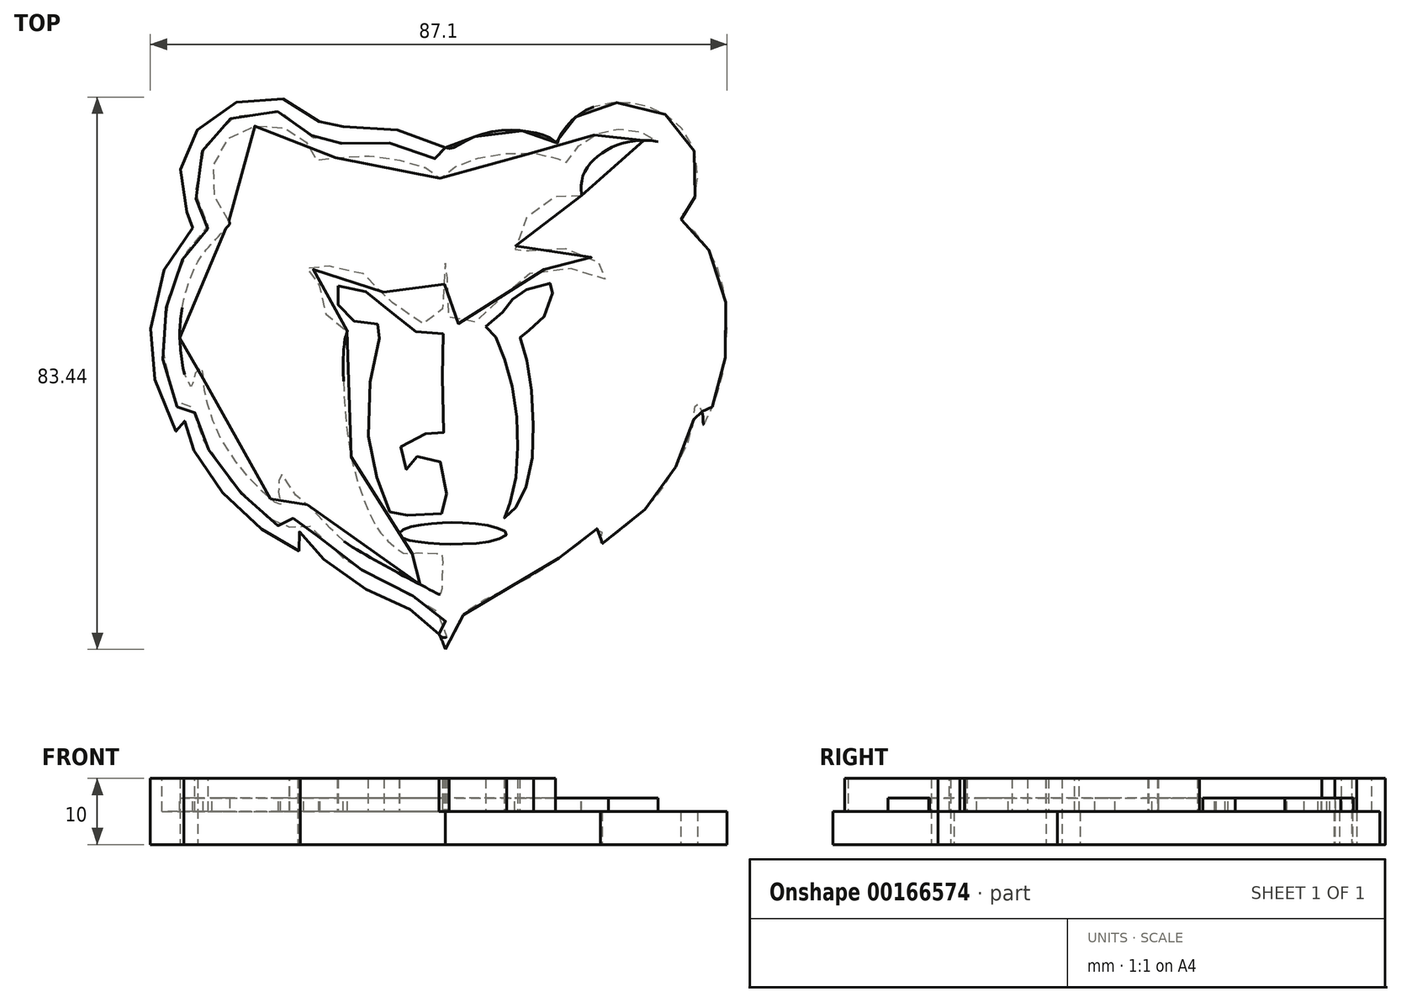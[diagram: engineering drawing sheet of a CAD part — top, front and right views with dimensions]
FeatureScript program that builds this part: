
annotation { "Feature Type Name" : "Feature", "Feature Type Description" : "" }
export const myFeature = defineFeature(function(context is Context, id is Id, definition is map)
    precondition{}
    {
        {
            var Q0;
            Q0=qCreatedBy(makeId("Top.planeOp"),FACE);
            var sketch = newSketch(context, id + "F0", { "sketchPlane" : qUnion([Q0])});
            skLineSegment(sketch, "E0", {"start": v(0, 41.26) * mm, "end": v(0, -52.03) * mm, "construction": true});
            skFitSpline(sketch, "E1", {"points": [v(0, 27.13) * mm, v(-4.89, 29.17) * mm, v(-10.68, 30.33) * mm, v(-16.3, 30.11) * mm, v(-17.96, 29.67) * mm, v(-18.3, 30.11) * mm, v(-20.17, 32.15) * mm, v(-23.48, 34.2) * mm, v(-27.3, 34.75) * mm, v(-32.15, 33.8) * mm, v(-36.17, 31.38) * mm, v(-38.93, 27.4) * mm, v(-39.93, 24.26) * mm, v(-39.87, 19.57) * mm, v(-38.93, 17.14) * mm, v(-38.1, 15.82) * mm, v(-37.39, 15.27) * mm, v(-38.16, 15.05) * mm, v(-40.75, 11.96) * mm, v(-43.84, 4.9) * mm, v(-44.56, -1.84) * mm, v(-44.12, -6.92) * mm, v(-41.75, -13.87) * mm, v(-40.04, -16.4) * mm, v(-39.54, -16.4) * mm, v(-39.65, -15.52) * mm, v(-39.32, -14.09) * mm, v(-39.1, -15.52) * mm, v(-38.1, -18.4) * mm, v(-35.57, -22.42) * mm, v(-31.81, -27.06) * mm, v(-27.4, -30.8) * mm, v(-23.76, -33.18) * mm, v(-21.94, -33.79) * mm, v(-22.16, -33.13) * mm, v(-22.32, -31.97) * mm, v(-22.1, -30.92) * mm, v(-21, -32.3) * mm, v(-18.74, -34.73) * mm, v(-14.6, -38.1) * mm, v(-9.9, -40.58) * mm, v(-5.6, -42.5) * mm, v(-2.68, -44.33) * mm, v(-0.97, -46.42) * mm, v(0, -48.69) * mm], "startDerivative": vector(-162.67, 75.76) * mm, "endDerivative": vector(42.07, -115.13) * mm});
            skFitSpline(sketch, "E2", {"points": [v(0, -48.69) * mm, v(1, -46.59) * mm, v(2.6, -43.61) * mm, v(5.27, -41.5) * mm, v(12.4, -37.98) * mm, v(16.97, -35) * mm, v(21.87, -31.35) * mm, v(22.98, -30.42) * mm, v(23.54, -30.8) * mm, v(23.6, -32.03) * mm, v(23.42, -32.84) * mm, v(25.52, -31.35) * mm, v(30.35, -27.32) * mm, v(33.39, -23.42) * mm, v(36.24, -18.4) * mm, v(37.49, -14.1) * mm, v(37.88, -11.34) * mm, v(38.1, -11.43) * mm, v(38.63, -12.26) * mm, v(38.94, -13.97) * mm, v(39.02, -14.76) * mm, v(40.47, -11.65) * mm, v(41.83, -7.31) * mm, v(42.5, -1.49) * mm, v(42.28, 4.04) * mm, v(40.8, 9.7) * mm, v(38.07, 13.97) * mm, v(35.8, 16.07) * mm, v(35.59, 16.42) * mm, v(35.63, 16.95) * mm, v(36.5, 17.78) * mm, v(37.82, 20.19) * mm, v(37.94, 24.7) * mm, v(37.11, 27.8) * mm, v(34.47, 31.27) * mm, v(30.13, 33.46) * mm, v(25.54, 33.92) * mm, v(21.74, 33) * mm, v(18.92, 31.06) * mm, v(17.1, 28.46) * mm, v(16.9, 27.8) * mm, v(15.99, 28.46) * mm, v(13.67, 29.33) * mm, v(10.33, 29.78) * mm, v(5.78, 29.24) * mm, v(2.35, 27.76) * mm, v(0.86, 27.01) * mm, v(0, 27.13) * mm], "startDerivative": vector(49.23, 102.83) * mm, "endDerivative": vector(-71.58, 21.7) * mm});
            skFitSpline(sketch, "E3", {"points": [v(0, 27.13) * mm, v(0.32, 26.7) * mm, v(0.53, 25.95) * mm, v(0.24, 25.3) * mm, v(-0.9, 25.22) * mm, v(-2.84, 26.07) * mm, v(-5.73, 27.13) * mm, v(-9.87, 28.03) * mm, v(-13.28, 28.07) * mm, v(-15.78, 27.78) * mm, v(-17.43, 27.45) * mm, v(-18.61, 27.33) * mm, v(-19.96, 28.65) * mm, v(-21.65, 30.58) * mm, v(-23.82, 32.04) * mm, v(-26.18, 32.7) * mm, v(-29.9, 32.41) * mm, v(-32.48, 31.5) * mm, v(-34.55, 29.87) * mm, v(-36.12, 27.74) * mm, v(-37.34, 25.12) * mm, v(-37.85, 21.65) * mm, v(-37.48, 18.46) * mm, v(-36.66, 16.5) * mm, v(-36, 15.61) * mm, v(-35.85, 15.05) * mm, v(-36.18, 14.62) * mm, v(-37.17, 13.8) * mm, v(-39.03, 11.41) * mm, v(-40.7, 8.1) * mm, v(-41.71, 4.92) * mm, v(-42.56, 0.72) * mm, v(-42.78, -2.61) * mm, v(-42.43, -6.62) * mm, v(-41.2, -10.52) * mm, v(-40.42, -12.14) * mm, v(-40.24, -12.18) * mm, v(-39.67, -11.66) * mm, v(-38.9, -11.5) * mm, v(-38.18, -12.27) * mm, v(-37.68, -13.36) * mm, v(-37.29, -14.98) * mm, v(-36.34, -17.54) * mm, v(-34.69, -20.14) * mm, v(-32.23, -23.5) * mm, v(-29.14, -26.86) * mm, v(-26.99, -28.72) * mm, v(-24.55, -30.58) * mm, v(-23.74, -31.1) * mm, v(-23.55, -31.02) * mm, v(-23.55, -30.02) * mm, v(-22.9, -28.81) * mm, v(-22.05, -28.65) * mm, v(-21, -29.44) * mm, v(-19.6, -31.16) * mm, v(-17.43, -33.45) * mm, v(-13.55, -36.17) * mm, v(-8.98, -38.6) * mm, v(-5.16, -40.51) * mm, v(-2.53, -41.94) * mm, v(-0.74, -43.42) * mm, v(0.17, -44.7) * mm, v(0.5, -45.67) * mm, v(0.36, -46.67) * mm, v(-0.4, -46.89) * mm, v(-0.97, -46.42) * mm], "startDerivative": vector(43.35, -47.73) * mm, "endDerivative": vector(-53.4, 65.08) * mm});
            skSolve(sketch);
        }
        {
            var Q0;
            Q0 = qSketchRegion(id + "F0", true);
            extrude(context, id + "F1", {"entities" : qUnion([Q0]), "depth" : 5 * mm});
        }
        {
            var Q0;
            {var subQ0=sQuery(id+"F0.wireOp",EDGE,"E3");Q0=makeQuery(id+"F0.imprint","IMPRINT",FACE,{"disambiguationData":[TD([[makeQuery(id+"F0.imprint","IMPRINT",EDGE,{"derivedFrom":subQ0}),-1.0]])]});}
            extrude(context, id + "F2", {"entities" : qUnion([Q0]), "operationType" : NewBodyOperationType.ADD, "depth" : 10 * mm});
        }
        {
            var Q0;
            Q0=makeQuery(id+"F1.opExtrude","CAP_FACE",FACE,{"disambiguationData":[OSD([sQuery(id+"F0.wireOp",EDGE,"E1"),sQuery(id+"F0.wireOp",EDGE,"E2")])],"isStart":false});
            var sketch = newSketch(context, id + "F3", { "sketchPlane" : qUnion([Q0])});
            skFitSpline(sketch, "E4", {"points": [v(-32.42, 15.69) * mm, v(-34.04, 17.77) * mm, v(-35.18, 21.16) * mm, v(-34.87, 24.96) * mm, v(-33.3, 28.03) * mm, v(-30.34, 29.96) * mm, v(-26.95, 30.53) * mm, v(-24.09, 30.01) * mm, v(-21.85, 28.69) * mm, v(-20.17, 26.92) * mm, v(-19.45, 25.48) * mm, v(-19.31, 25.13) * mm, v(-18.15, 25.32) * mm, v(-14.71, 25.8) * mm, v(-10.96, 25.85) * mm, v(-7.32, 25.32) * mm, v(-4.6, 24.65) * mm, v(-2.42, 23.81) * mm, v(-1.12, 22.85) * mm, v(-0.65, 22.46) * mm, v(-0.23, 22.87) * mm, v(1.03, 23.97) * mm, v(2.93, 24.93) * mm, v(5.36, 25.68) * mm, v(8.07, 26.15) * mm, v(11.57, 26.34) * mm, v(14.22, 26.2) * mm, v(16.32, 25.76) * mm, v(17.47, 25.13) * mm, v(17.89, 24.74) * mm, v(18.08, 24.57) * mm, v(18.47, 25.2) * mm, v(19.3, 26.42) * mm, v(20.55, 27.77) * mm, v(22.13, 28.85) * mm, v(23.68, 29.52) * mm, v(25.5, 29.9) * mm, v(27.57, 29.9) * mm, v(29.35, 29.58) * mm, v(31.16, 28.76) * mm, v(32.13, 28.06) * mm, v(31.46, 28.15) * mm, v(30.14, 28.24) * mm, v(27.77, 28.03) * mm, v(25.38, 27.3) * mm, v(23.07, 25.87) * mm, v(21.55, 24.35) * mm, v(20.7, 22.56) * mm, v(20.52, 20.75) * mm, v(20.55, 19.88) * mm, v(20.38, 19.61) * mm, v(19.2, 19.82) * mm, v(17.04, 19.79) * mm, v(14.68, 18.91) * mm, v(12.75, 17.16) * mm, v(11.4, 15.2) * mm, v(10.64, 12.6) * mm, v(10.52, 11.26) * mm, v(10.52, 10.57) * mm, v(11.03, 10.82) * mm, v(12.56, 11.53) * mm, v(15.19, 12.05) * mm, v(17.91, 11.95) * mm, v(20.6, 11.24) * mm, v(22.8, 10.06) * mm, v(24.28, 8.56) * mm, v(24.6, 7.65) * mm, v(24.55, 7.2) * mm, v(23.6, 7.45) * mm, v(21.28, 8.34) * mm, v(18.3, 8.93) * mm, v(14.72, 8.66) * mm, v(11.62, 7.48) * mm, v(9.68, 5.7) * mm, v(7.79, 3.67) * mm, v(5.72, 1.6) * mm, v(4.05, 0.64) * mm, v(1.94, 0.54) * mm, v(0.76, 1.11) * mm, v(0.39, 2.34) * mm, v(0.32, 5.14) * mm, v(0.3, 10) * mm, v(0.22, 11) * mm, v(0, 9.98) * mm, v(-0.2, 5.12) * mm, v(-0.52, 2.29) * mm, v(-1.06, 1.2) * mm, v(-2.27, 0.6) * mm, v(-4.38, 0.7) * mm, v(-6.76, 2.27) * mm, v(-9.15, 5.07) * mm, v(-11.56, 7.45) * mm, v(-13.74, 8.68) * mm, v(-16.13, 9.12) * mm, v(-18.8, 9.22) * mm, v(-21.17, 9.07) * mm, v(-21.39, 8.98) * mm, v(-20.11, 8.75) * mm, v(-19.32, 8.34) * mm, v(-18.98, 7.7) * mm, v(-19.08, 5.83) * mm, v(-19, 4.16) * mm, v(-18.37, 2.51) * mm, v(-17.4, 1.04) * mm, v(-16.42, 0) * mm, v(-15.12, -0.49) * mm, v(-14.83, -0.49) * mm, v(-15.02, -1.3) * mm, v(-15.4, -3.95) * mm, v(-15.4, -7.91) * mm, v(-15.08, -13.45) * mm, v(-14.42, -18.64) * mm, v(-13.2, -23.5) * mm, v(-11.2, -28.67) * mm, v(-9.59, -31.34) * mm, v(-7.55, -33.32) * mm, v(-6, -34.25) * mm, v(-4.7, -34.12) * mm, v(-3.06, -34.15) * mm, v(-0.95, -34.19) * mm, v(-0.52, -34.34) * mm, v(-0.48, -37.25) * mm, v(-0.6, -40.2) * mm, v(-0.83, -40.38) * mm, v(-2.51, -39.6) * mm, v(-6.55, -37.47) * mm, v(-11.05, -34.96) * mm, v(-15.23, -32.4) * mm, v(-18.5, -29.26) * mm, v(-21.05, -26.7) * mm, v(-22.9, -25.05) * mm, v(-24.15, -22.97) * mm, v(-24.86, -22.23) * mm, v(-25.1, -22.97) * mm, v(-25.23, -24.5) * mm, v(-24.92, -26.6) * mm, v(-24.92, -26.97) * mm, v(-26.72, -25.7) * mm, v(-29.4, -23.04) * mm, v(-33.75, -17.21) * mm, v(-35.7, -12.38) * mm, v(-36.38, -9.63) * mm, v(-36.6, -6.62) * mm, v(-36.69, -6.13) * mm, v(-37.37, -6.31) * mm, v(-37.96, -7.52) * mm, v(-38.17, -8.76) * mm, v(-38.2, -9.13) * mm, v(-38.92, -8.36) * mm, v(-39.85, -4.76) * mm, v(-40.13, -1.02) * mm, v(-39.85, 2.3) * mm, v(-38.86, 6.5) * mm, v(-37.1, 10.35) * mm, v(-35.3, 12.6) * mm, v(-33.13, 14.93) * mm], "startDerivative": vector(-236.1, 263.18) * mm, "endDerivative": vector(281.53, 298.53) * mm});
            skFitSpline(sketch, "E5", {"points": [v(-33.13, 14.93) * mm, v(-32.42, 15.69) * mm], "startDerivative": vector(0.7, 0.76) * mm, "endDerivative": vector(0.7, 0.76) * mm});
            skArc(sketch, "E6.filletArc", {"start": v(-32.73, 15.36) * mm, "mid": v(-32.6, 15.69) * mm, "end": v(-32.72, 16.03) * mm});
            skSolve(sketch);
        }
        {
            var Q0;
            Q0 = qSketchRegion(id + "F3", true);
            extrude(context, id + "F4", {"entities" : qUnion([Q0]), "operationType" : NewBodyOperationType.ADD, "depth" : 2 * mm});
        }
        {
            var Q0;
            Q0=makeQuery(id+"F1.opExtrude","CAP_FACE",FACE,{"disambiguationData":[OSD([sQuery(id+"F0.wireOp",EDGE,"E1"),sQuery(id+"F0.wireOp",EDGE,"E2")])],"isStart":false});
            var sketch = newSketch(context, id + "F5", { "sketchPlane" : qUnion([Q0])});
            skFitSpline(sketch, "E7", {"points": [v(-16.18, 6.26) * mm, v(-15.05, 6.28) * mm, v(-12.77, 5.66) * mm, v(-10.48, 4.54) * mm, v(-8.45, 2.58) * mm, v(-6.45, 0.67) * mm, v(-4.9, -0.47) * mm, v(-2.9, -1.02) * mm, v(-0.55, -1.05) * mm, v(-0.35, -1.01) * mm, v(-0.4, -3.03) * mm, v(-0.43, -10.49) * mm, v(-0.23, -16.35) * mm, v(-0.22, -16.58) * mm, v(-0.85, -16.3) * mm, v(-3.02, -16.14) * mm, v(-5.05, -16.55) * mm, v(-6.58, -17.8) * mm, v(-6.92, -19.27) * mm, v(-6.55, -20.7) * mm, v(-5.77, -21.6) * mm, v(-5.59, -21.64) * mm, v(-5.45, -20.86) * mm, v(-4.64, -19.77) * mm, v(-3.45, -19.33) * mm, v(-1.85, -19.46) * mm, v(-0.68, -20.5) * mm, v(-0.2, -21.71) * mm, v(0.2, -25.49) * mm, v(0.19, -27.61) * mm, v(0, -27.96) * mm, v(-0.4, -28.12) * mm, v(-2.68, -28.38) * mm, v(-5.63, -28.44) * mm, v(-7.22, -28.44) * mm, v(-7.92, -28.48) * mm, v(-8.08, -28.44) * mm, v(-8.6, -27.46) * mm, v(-9.82, -24.44) * mm, v(-10.92, -20.68) * mm, v(-11.63, -16.27) * mm, v(-11.5, -9.23) * mm, v(-10.5, -3.46) * mm, v(-9.67, -0.96) * mm, v(-9.3, 0) * mm, v(-9.32, 0.3) * mm, v(-10.26, 0.44) * mm, v(-11.52, 0.37) * mm, v(-12.95, 0.47) * mm, v(-14.36, 1.33) * mm, v(-15.42, 2.17) * mm, v(-15.99, 2.8) * mm, v(-16.32, 4.34) * mm, v(-16.23, 5.23) * mm, v(-16.22, 6.02) * mm, v(-16.18, 6.26) * mm]});
            skFitSpline(sketch, "E8", {"points": [v(-5.15, -30.18) * mm, v(-2.92, -29.79) * mm, v(-0.34, -29.54) * mm, v(1.7, -29.55) * mm, v(5.3, -29.8) * mm, v(8, -30.38) * mm, v(9.06, -30.88) * mm, v(9.27, -31.3) * mm, v(8.3, -31.9) * mm, v(5.73, -32.55) * mm, v(1.72, -32.77) * mm, v(-1.13, -32.75) * mm, v(-3.8, -32.46) * mm, v(-5.4, -32.22) * mm, v(-6.62, -31.78) * mm, v(-7, -31.22) * mm, v(-6.55, -30.67) * mm, v(-5.15, -30.18) * mm]});
            skFitSpline(sketch, "E9", {"points": [v(6.08, 0.08) * mm, v(7.87, 1.63) * mm, v(9.21, 2.89) * mm, v(9.94, 3.94) * mm, v(10.5, 4.7) * mm, v(11.78, 5.46) * mm, v(14.27, 6.42) * mm, v(16.48, 6.64) * mm, v(16.62, 6.5) * mm, v(16.1, 4.87) * mm, v(15.17, 2.01) * mm, v(13.5, 0.05) * mm, v(12.3, -0.62) * mm, v(11.39, -1.02) * mm, v(11.25, -1.3) * mm, v(11.74, -3) * mm, v(12.62, -6.55) * mm, v(13.16, -11.34) * mm, v(13.28, -17.1) * mm, v(12.83, -21.76) * mm, v(11.7, -25.32) * mm, v(10.68, -27.26) * mm, v(9.64, -28.46) * mm, v(8.94, -28.83) * mm, v(9.02, -28.25) * mm, v(9.68, -26.76) * mm, v(10.47, -23.95) * mm, v(10.88, -19.82) * mm, v(10.88, -15.31) * mm, v(10.47, -11.01) * mm, v(9.53, -6.45) * mm, v(8.5, -3.73) * mm, v(7.52, -1.28) * mm, v(6.87, -0.35) * mm, v(6.08, 0.08) * mm]});
            skSolve(sketch);
        }
        {
            var Q0;
            Q0 = qSketchRegion(id + "F5", true);
            extrude(context, id + "F6", {"entities" : qUnion([Q0]), "operationType" : NewBodyOperationType.ADD, "depth" : 5 * mm});
        }
    });
